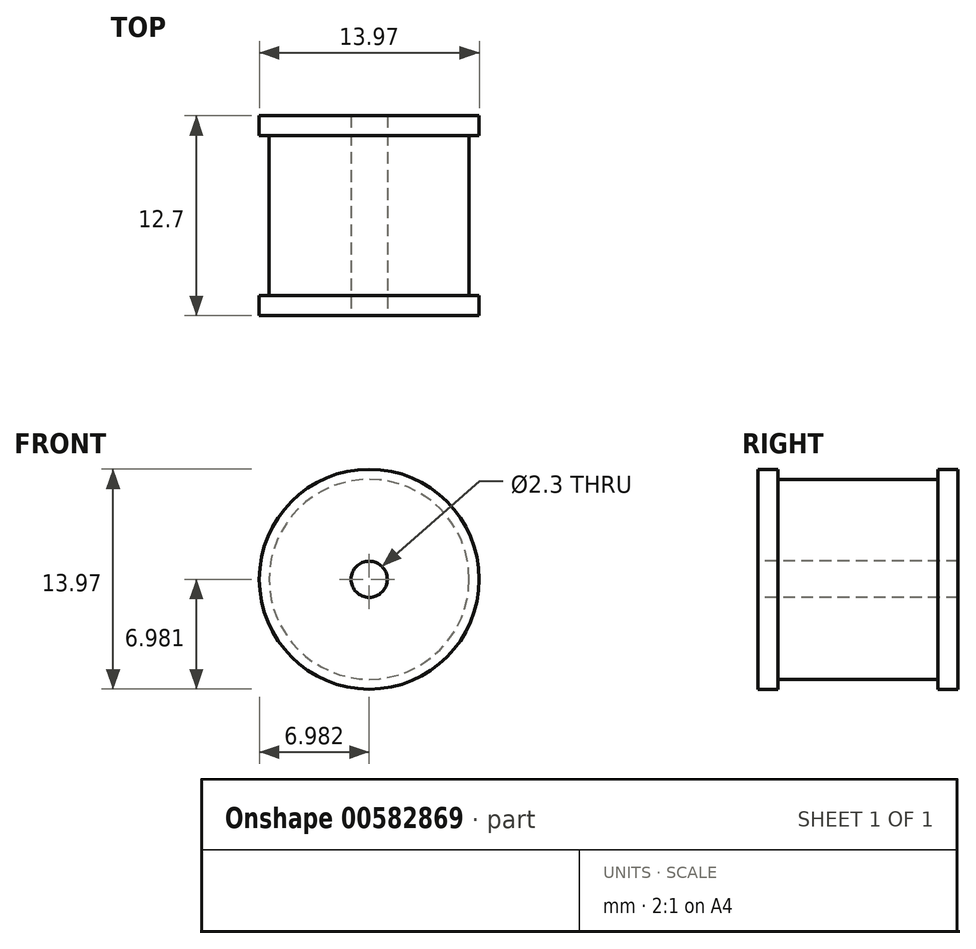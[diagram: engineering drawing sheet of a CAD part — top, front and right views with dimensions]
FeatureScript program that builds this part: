
annotation { "Feature Type Name" : "Feature", "Feature Type Description" : "" }
export const myFeature = defineFeature(function(context is Context, id is Id, definition is map)
    precondition{}
    {
        {
            var Q0;
            Q0=qCreatedBy(makeId("Front.planeOp"),FACE);
            var sketch = newSketch(context, id + "F0", { "sketchPlane" : qUnion([Q0])});
            skCircle(sketch, "E0", {"center": v(-8.39, 6.65) * mm, "radius": 6.35 * mm});
            skSolve(sketch);
        }
        {
            var Q0;
            Q0 = qSketchRegion(id + "F0", true);
            extrude(context, id + "F1", {"entities" : qUnion([Q0]), "depth" : 12.7 * mm, "offsetDistance" : 25.4 * mm});
        }
        {
            var Q0;
            Q0=makeQuery(id+"F1.opExtrude","CAP_FACE",FACE,{"disambiguationData":[OSD([sQuery(id+"F0.wireOp",EDGE,"E0")])],"isStart":false});
            var sketch = newSketch(context, id + "F2", { "sketchPlane" : qUnion([Q0])});
            skCircle(sketch, "E1", {"center": v(-8.39, 6.65) * mm, "radius": 6.99 * mm});
            skSolve(sketch);
        }
        {
            var Q0;
            Q0 = qSketchRegion(id + "F2", true);
            extrude(context, id + "F3", {"entities" : qUnion([Q0]), "operationType" : NewBodyOperationType.ADD, "oppositeDirection" : true, "depth" : 1.27 * mm, "offsetDistance" : 25.4 * mm});
        }
        {
            var Q0;
            Q0=qCreatedBy(makeId("Front.planeOp"),FACE);
            var sketch = newSketch(context, id + "F4", { "sketchPlane" : qUnion([Q0])});
            skCircle(sketch, "E2", {"center": v(-8.39, 6.65) * mm, "radius": 6.99 * mm});
            skSolve(sketch);
        }
        {
            var Q0;
            Q0 = qSketchRegion(id + "F4", true);
            extrude(context, id + "F5", {"entities" : qUnion([Q0]), "operationType" : NewBodyOperationType.ADD, "depth" : 1.27 * mm, "offsetDistance" : 25.4 * mm});
        }
        {
            var Q0;
            Q0=makeQuery(id+"F3.boolean.opBoolean","MERGE",FACE,{"derivedFrom":[makeQuery(id+"F1.opExtrude","CAP_FACE",FACE,{"disambiguationData":[OSD([sQuery(id+"F0.wireOp",EDGE,"E0")])],"isStart":false}),makeQuery(id+"F3.opExtrude","CAP_FACE",FACE,{"disambiguationData":[OSD([sQuery(id+"F2.wireOp",EDGE,"E1")])],"isStart":true})]});
            var sketch = newSketch(context, id + "F6", { "sketchPlane" : qUnion([Q0])});
            skCircle(sketch, "E3", {"center": v(-8.39, 6.65) * mm, "radius": 1.15 * mm});
            skSolve(sketch);
        }
        {
            var Q0;
            Q0 = qSketchRegion(id + "F6", true);
            extrude(context, id + "F7", {"entities" : qUnion([Q0]), "operationType" : NewBodyOperationType.REMOVE, "oppositeDirection" : true, "depth" : 25.4 * mm, "offsetDistance" : 25.4 * mm});
        }
    });
